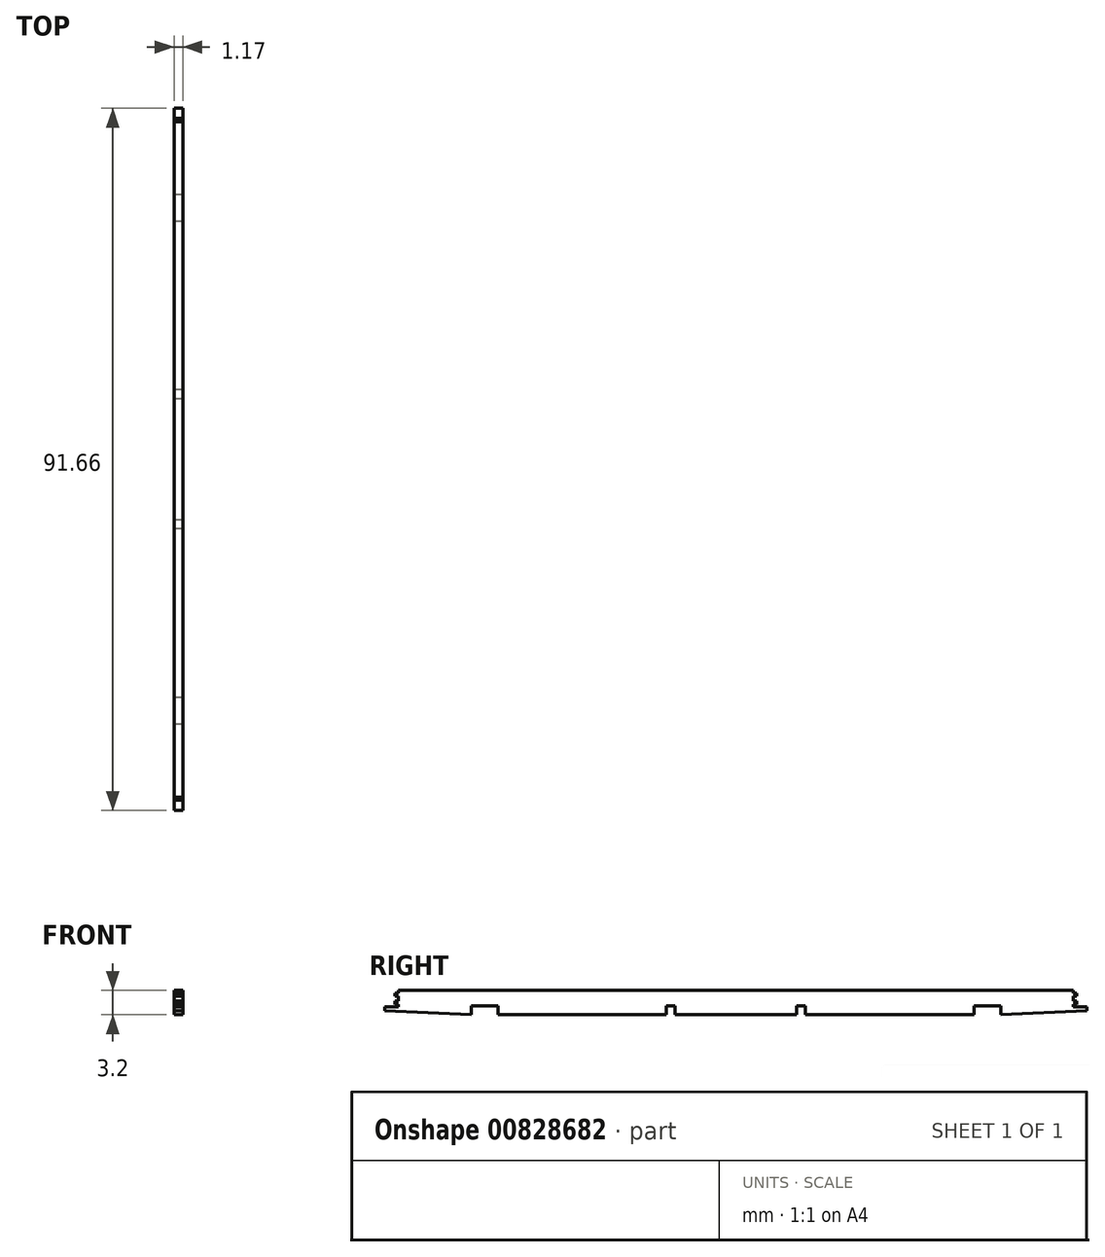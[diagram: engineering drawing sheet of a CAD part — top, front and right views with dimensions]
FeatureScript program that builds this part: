
annotation { "Feature Type Name" : "Feature", "Feature Type Description" : "" }
export const myFeature = defineFeature(function(context is Context, id is Id, definition is map)
    precondition{}
    {
        {
            var Q0;
            Q0=qCreatedBy(makeId("Right.planeOp"),FACE);
            var sketch = newSketch(context, id + "F0", { "sketchPlane" : qUnion([Q0])});
            skLineSegment(sketch, "E0", {"start": v(0, 0) * mm, "end": v(0, 1.16) * mm});
            skLineSegment(sketch, "E1", {"start": v(0, 1.16) * mm, "end": v(-3.5, 1.16) * mm});
            skLineSegment(sketch, "E2", {"start": v(-3.5, 1.16) * mm, "end": v(-3.5, 0) * mm});
            skLineSegment(sketch, "E3", {"start": v(-13.01, 1.04) * mm, "end": v(-13.01, 1.39) * mm});
            skLineSegment(sketch, "E4", {"start": v(-13.01, 3.2) * mm, "end": v(75.17, 3.2) * mm});
            skLineSegment(sketch, "E5", {"start": v(-13.01, 3.2) * mm, "end": v(-13.01, 2.85) * mm});
            skLineSegment(sketch, "E6", {"start": v(-13.01, 2.85) * mm, "end": v(-13.43, 2.85) * mm});
            skLineSegment(sketch, "E7", {"start": v(-13.43, 2.85) * mm, "end": v(-13.43, 2.41) * mm});
            skLineSegment(sketch, "E8", {"start": v(-13.43, 2.41) * mm, "end": v(-13.01, 2.41) * mm});
            skLineSegment(sketch, "E9", {"start": v(-13.01, 2.41) * mm, "end": v(-13.01, 1.82) * mm});
            skLineSegment(sketch, "E10", {"start": v(-13.01, 1.82) * mm, "end": v(-13.43, 1.82) * mm});
            skLineSegment(sketch, "E11", {"start": v(-13.43, 1.82) * mm, "end": v(-13.43, 1.39) * mm});
            skLineSegment(sketch, "E12", {"start": v(-13.43, 1.39) * mm, "end": v(-13.01, 1.39) * mm});
            skLineSegment(sketch, "E13", {"start": v(-13.01, 1.39) * mm, "end": v(-13.01, 1.04) * mm});
            skLineSegment(sketch, "E14", {"start": v(-13.01, 1.04) * mm, "end": v(-14.75, 1.04) * mm});
            skLineSegment(sketch, "E15", {"start": v(-14.75, 1.04) * mm, "end": v(-14.75, 0.54) * mm});
            skLineSegment(sketch, "E16", {"start": v(-14.75, 0.54) * mm, "end": v(-3.5, 0) * mm});
            skLineSegment(sketch, "E17.trimOffspring", {"start": v(-13.01, 1.82) * mm, "end": v(-13.01, 2.41) * mm});
            skLineSegment(sketch, "E18.trimOffspring", {"start": v(-13.01, 2.85) * mm, "end": v(-13.01, 3.2) * mm});
            skLineSegment(sketch, "E19.MirrorCS", {"start": v(75.17, 3.2) * mm, "end": v(75.17, 2.85) * mm});
            skLineSegment(sketch, "E20.MirrorCS", {"start": v(75.17, 2.85) * mm, "end": v(75.59, 2.85) * mm});
            skLineSegment(sketch, "E21.MirrorCS", {"start": v(75.59, 2.85) * mm, "end": v(75.59, 2.41) * mm});
            skLineSegment(sketch, "E22.MirrorCS", {"start": v(75.59, 2.41) * mm, "end": v(75.17, 2.41) * mm});
            skLineSegment(sketch, "E23.MirrorCS", {"start": v(75.17, 1.82) * mm, "end": v(75.17, 2.41) * mm});
            skLineSegment(sketch, "E24.MirrorCS", {"start": v(75.17, 1.82) * mm, "end": v(75.59, 1.82) * mm});
            skLineSegment(sketch, "E25.MirrorCS", {"start": v(75.59, 1.82) * mm, "end": v(75.59, 1.39) * mm});
            skLineSegment(sketch, "E26.MirrorCS", {"start": v(75.59, 1.39) * mm, "end": v(75.17, 1.39) * mm});
            skLineSegment(sketch, "E27.MirrorCS", {"start": v(75.17, 1.04) * mm, "end": v(75.17, 1.39) * mm});
            skLineSegment(sketch, "E28.MirrorCS", {"start": v(75.17, 1.04) * mm, "end": v(76.9, 1.04) * mm});
            skLineSegment(sketch, "E29.MirrorCS", {"start": v(76.9, 1.04) * mm, "end": v(76.9, 0.54) * mm});
            skLineSegment(sketch, "E30.MirrorCS", {"start": v(76.9, 0.54) * mm, "end": v(65.66, 0) * mm});
            skLineSegment(sketch, "E31.MirrorCS", {"start": v(65.66, 1.16) * mm, "end": v(65.66, 0) * mm});
            skLineSegment(sketch, "E32.MirrorCS", {"start": v(62.16, 1.16) * mm, "end": v(65.66, 1.16) * mm});
            skLineSegment(sketch, "E33.MirrorCS", {"start": v(62.16, 0) * mm, "end": v(62.16, 1.16) * mm});
            skLineSegment(sketch, "E34", {"start": v(0, 0) * mm, "end": v(22, 0) * mm});
            skLineSegment(sketch, "E35", {"start": v(22, 0) * mm, "end": v(22, 1.17) * mm});
            skLineSegment(sketch, "E36", {"start": v(22, 1.17) * mm, "end": v(23.16, 1.17) * mm});
            skLineSegment(sketch, "E37", {"start": v(23.16, 1.17) * mm, "end": v(23.16, 0) * mm});
            skLineSegment(sketch, "E38.MirrorCS", {"start": v(62.16, 0) * mm, "end": v(40.17, 0) * mm});
            skLineSegment(sketch, "E39.MirrorCS", {"start": v(40.17, 1.17) * mm, "end": v(39, 1.17) * mm});
            skLineSegment(sketch, "E40.MirrorCS", {"start": v(40.17, 0) * mm, "end": v(40.17, 1.17) * mm});
            skLineSegment(sketch, "E41.MirrorCS", {"start": v(39, 1.17) * mm, "end": v(39, 0) * mm});
            skLineSegment(sketch, "E42", {"start": v(39, 0) * mm, "end": v(23.16, 0) * mm});
            skSolve(sketch);
        }
        {
            var Q0;
            Q0=makeQuery(id+"F0.imprint","IMPRINT",FACE,{"disambiguationData":[TD([[makeQuery(id+"F0.imprint","IMPRINT",EDGE,{"derivedFrom":sQuery(id+"F0.wireOp",EDGE,"E0")}),-1.0]])]});
            extrude(context, id + "F1", {"entities" : qUnion([Q0]), "depth" : 1.17 * mm, "offsetDistance" : 25.4 * mm});
        }
    });
